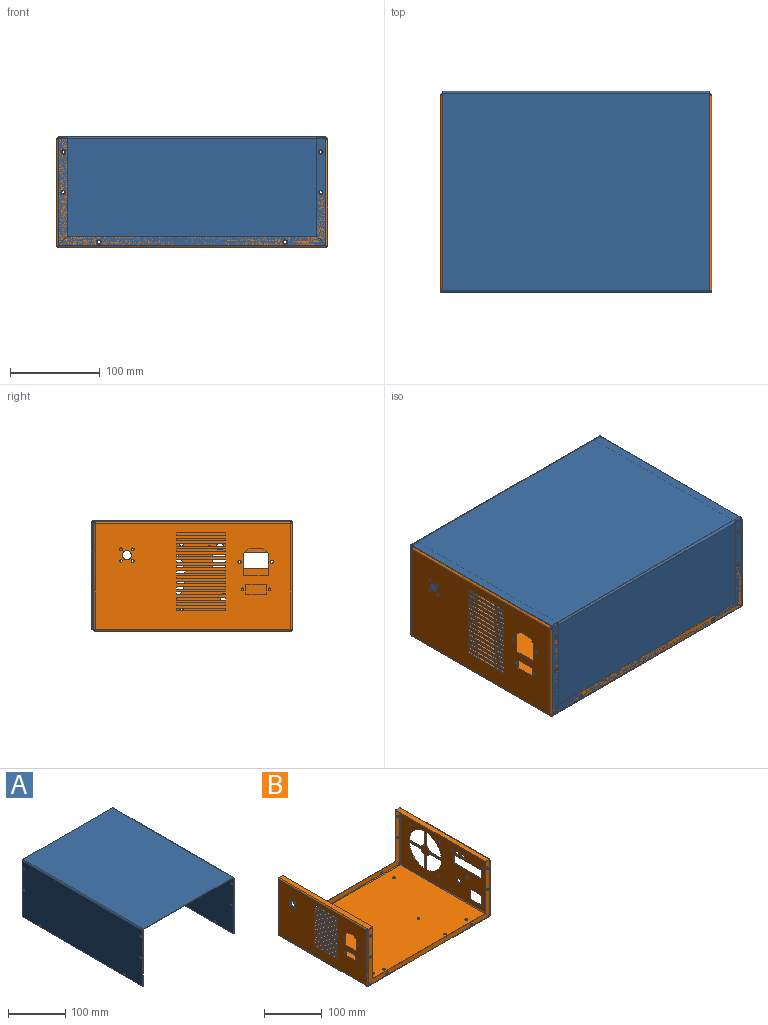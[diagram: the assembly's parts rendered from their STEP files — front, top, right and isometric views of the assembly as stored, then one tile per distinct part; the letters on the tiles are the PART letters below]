
ASSEMBLY  parts=2 mates=1
PART A: 34 faces, bbox 224.5x297.4x121 mm
  f0: plane 219.9x1mm, normal (0,-1,0), area 219.9mm2, adj f2,f3,f16,f31
  f1: plane 219.9x1mm, normal (0,1,0), area 219.9mm2, adj f2,f3,f15,f30
  f2: plane 297.4x219.9mm, normal (0,0,1), area 65398.3mm2, adj f0,f1,f17,f32
  f3: plane 297.4x219.9mm, normal (0,0,-1), area 65398.3mm2, adj f0,f1,f18,f33
  f4: plane 118.7x1mm, normal (0,-1,0), area 118.7mm2, adj f12,f13,f14,f16
  f5: plane 118.7x1mm, normal (0,1,0), area 118.7mm2, adj f12,f13,f14,f15
  f6: cylinder r=1.75mm len=3.5mm, axis (-1,0,0), area 11mm2, adj f13,f14
  f7: cylinder r=1.75mm len=3.5mm, axis (-1,0,0), area 11mm2, adj f13,f14
  f8: cylinder r=1.75mm len=3.5mm, axis (-1,0,0), area 11mm2, adj f13,f14
  f9: cylinder r=1.75mm len=3.5mm, axis (-1,0,0), area 11mm2, adj f13,f14
  f10: cylinder r=1.75mm len=3.5mm, axis (-1,0,0), area 11mm2, adj f13,f14
  f11: cylinder r=1.75mm len=3.5mm, axis (-1,0,0), area 11mm2, adj f13,f14
  f12: plane 297.4x1mm, normal (0,0,-1), area 297.4mm2, adj f4,f5,f13,f14
  f13: plane 297.4x118.7mm, normal (-1,0,0), area 35243.7mm2, adj f4,f5,f6,f7,f8,f9,f10,f11
  f14: plane 297.4x118.7mm, normal (1,0,0), area 35243.7mm2, adj f4,f5,f6,f7,f8,f9,f10,f11
  f15: plane 2.3x2.3mm, normal (0,1,0), area 2.8mm2, adj f1,f5,f17,f18
  f16: plane 2.3x2.3mm, normal (0,-1,0), area 2.8mm2, adj f0,f4,f17,f18
  f17: cylinder r=2.3mm len=297.4mm, axis (0,1,0), area 1074.5mm2, adj f2,f13,f15,f16
  f18: cylinder r=1.3mm len=297.4mm, axis (0,1,0), area 607.3mm2, adj f3,f14,f15,f16
  f19: plane 118.7x1mm, normal (0,-1,0), area 118.7mm2, adj f20,f28,f29,f31
  f20: plane 297.4x1mm, normal (0,0,-1), area 297.4mm2, adj f19,f21,f28,f29
  f21: plane 118.7x1mm, normal (0,1,0), area 118.7mm2, adj f20,f28,f29,f30
  f22: cylinder r=1.75mm len=3.5mm, axis (-1,0,0), area 11mm2, adj f28,f29
  f23: cylinder r=1.75mm len=3.5mm, axis (-1,0,0), area 11mm2, adj f28,f29
  f24: cylinder r=1.75mm len=3.5mm, axis (-1,0,0), area 11mm2, adj f28,f29
  f25: cylinder r=1.75mm len=3.5mm, axis (-1,0,0), area 11mm2, adj f28,f29
  f26: cylinder r=1.75mm len=3.5mm, axis (-1,0,0), area 11mm2, adj f28,f29
  f27: cylinder r=1.75mm len=3.5mm, axis (-1,0,0), area 11mm2, adj f28,f29
  f28: plane 297.4x118.7mm, normal (1,0,0), area 35243.7mm2, adj f19,f20,f21,f22,f23,f24,f25,f26
  f29: plane 297.4x118.7mm, normal (-1,0,0), area 35243.7mm2, adj f19,f20,f21,f22,f23,f24,f25,f26
  f30: plane 2.3x2.3mm, normal (0,1,0), area 2.8mm2, adj f1,f21,f32,f33
  f31: plane 2.3x2.3mm, normal (0,-1,0), area 2.8mm2, adj f0,f19,f32,f33
  f32: cylinder r=2.3mm len=297.4mm, axis (0,1,0), area 1074.5mm2, adj f2,f28,f30,f31
  f33: cylinder r=1.3mm len=297.4mm, axis (0,1,0), area 607.3mm2, adj f3,f29,f30,f31
PART B: 235 faces, bbox 302x222x122 mm
  f0: plane 1x0.01mm, normal (0,-1,0), area 0mm2, adj f82,f83,f85,f219
  f1: plane 1x0.01mm, normal (0,1,0), area 0mm2, adj f135,f174,f175,f195
  f2: plane 11.1x1mm, normal (0,1,0), area 11.1mm2, adj f3,f81,f82,f83
  f3: plane 22.3x1mm, normal (0,0,1), area 22.3mm2, adj f2,f4,f82,f83
  f4: plane 11.1x1mm, normal (0,-1,0), area 11.1mm2, adj f3,f81,f82,f83
  f5: plane 15.5x1mm, normal (0,0,-1), area 15.5mm2, adj f6,f80,f82,f83
  f6: plane 6x6mm, normal (0,0.71,-0.71), area 8.5mm2, adj f5,f7,f82,f83
  f7: plane 24x1mm, normal (0,1,0), area 24mm2, adj f6,f8,f82,f83
  f8: plane 27.5x1mm, normal (0,0,1), area 27.5mm2, adj f7,f9,f82,f83
  f9: plane 24x1mm, normal (0,-1,0), area 24mm2, adj f8,f80,f82,f83
  f10: plane 3x1mm, normal (0,-1,0), area 3mm2, adj f11,f79,f82,f83
  f11: plane 55x1mm, normal (0,0,-1), area 55mm2, adj f10,f12,f82,f83
  f12: plane 3x1mm, normal (0,1,0), area 3mm2, adj f11,f79,f82,f83
  f13: plane 3x1mm, normal (0,-1,0), area 3mm2, adj f14,f78,f82,f83
  f14: plane 55x1mm, normal (0,0,-1), area 55mm2, adj f13,f15,f82,f83
  f15: plane 3x1mm, normal (0,1,0), area 3mm2, adj f14,f78,f82,f83
  f16: plane 3x1mm, normal (0,-1,0), area 3mm2, adj f17,f77,f82,f83
  f17: plane 55x1mm, normal (0,0,-1), area 55mm2, adj f16,f18,f82,f83
  f18: plane 3x1mm, normal (0,1,0), area 3mm2, adj f17,f77,f82,f83
  f19: plane 3x1mm, normal (0,-1,0), area 3mm2, adj f20,f76,f82,f83
  f20: plane 55x1mm, normal (0,0,-1), area 55mm2, adj f19,f21,f82,f83
  f21: plane 3x1mm, normal (0,1,0), area 3mm2, adj f20,f76,f82,f83
  f22: plane 3x1mm, normal (0,-1,0), area 3mm2, adj f23,f75,f82,f83
  f23: plane 55x1mm, normal (0,0,-1), area 55mm2, adj f22,f24,f82,f83
  f24: plane 3x1mm, normal (0,1,0), area 3mm2, adj f23,f75,f82,f83
  f25: plane 3x1mm, normal (0,-1,0), area 3mm2, adj f26,f74,f82,f83
  f26: plane 55x1mm, normal (0,0,-1), area 55mm2, adj f25,f27,f82,f83
  f27: plane 3x1mm, normal (0,1,0), area 3mm2, adj f26,f74,f82,f83
  f28: plane 3x1mm, normal (0,-1,0), area 3mm2, adj f29,f73,f82,f83
  f29: plane 55x1mm, normal (0,0,-1), area 55mm2, adj f28,f30,f82,f83
  f30: plane 3x1mm, normal (0,1,0), area 3mm2, adj f29,f73,f82,f83
  f31: plane 3x1mm, normal (0,-1,0), area 3mm2, adj f32,f72,f82,f83
  f32: plane 55x1mm, normal (0,0,-1), area 55mm2, adj f31,f33,f82,f83
  f33: plane 3x1mm, normal (0,1,0), area 3mm2, adj f32,f72,f82,f83
  f34: plane 3x1mm, normal (0,-1,0), area 3mm2, adj f35,f71,f82,f83
  f35: plane 55x1mm, normal (0,0,-1), area 55mm2, adj f34,f36,f82,f83
  f36: plane 3x1mm, normal (0,1,0), area 3mm2, adj f35,f71,f82,f83
  f37: plane 3x1mm, normal (0,-1,0), area 3mm2, adj f38,f70,f82,f83
  f38: plane 55x1mm, normal (0,0,-1), area 55mm2, adj f37,f39,f82,f83
  f39: plane 3x1mm, normal (0,1,0), area 3mm2, adj f38,f70,f82,f83
  f40: plane 3x1mm, normal (0,-1,0), area 3mm2, adj f41,f69,f82,f83
  f41: plane 55x1mm, normal (0,0,-1), area 55mm2, adj f40,f42,f82,f83
  f42: plane 3x1mm, normal (0,1,0), area 3mm2, adj f41,f69,f82,f83
  f43: plane 3x1mm, normal (0,-1,0), area 3mm2, adj f44,f68,f82,f83
  f44: plane 55x1mm, normal (0,0,-1), area 55mm2, adj f43,f45,f82,f83
  f45: plane 3x1mm, normal (0,1,0), area 3mm2, adj f44,f68,f82,f83
  f46: plane 3x1mm, normal (0,-1,0), area 3mm2, adj f47,f67,f82,f83
  f47: plane 55x1mm, normal (0,0,-1), area 55mm2, adj f46,f48,f82,f83
  f48: plane 3x1mm, normal (0,1,0), area 3mm2, adj f47,f67,f82,f83
  f49: plane 3x1mm, normal (0,-1,0), area 3mm2, adj f50,f66,f82,f83
  f50: plane 55x1mm, normal (0,0,-1), area 55mm2, adj f49,f51,f82,f83
  f51: plane 3x1mm, normal (0,1,0), area 3mm2, adj f50,f66,f82,f83
  f52: plane 55x1mm, normal (0,0,1), area 55mm2, adj f53,f65,f82,f83
  f53: plane 3x1mm, normal (0,-1,0), area 3mm2, adj f52,f54,f82,f83
  f54: plane 55x1mm, normal (0,0,-1), area 55mm2, adj f53,f65,f82,f83
  f55: plane 1x0.01mm, normal (0,1,0), area 0mm2, adj f82,f83,f84,f231
  f56: cylinder r=1.4mm len=2.8mm, axis (-1,0,0), area 8.8mm2, adj f82,f83
  f57: cylinder r=1.4mm len=2.8mm, axis (-1,0,0), area 8.8mm2, adj f82,f83
  f58: cylinder r=1.5mm len=3mm, axis (-1,0,0), area 9.4mm2, adj f82,f83
  f59: cylinder r=1.5mm len=3mm, axis (-1,0,0), area 9.4mm2, adj f82,f83
  f60: cylinder r=1.5mm len=3mm, axis (-1,0,0), area 9.4mm2, adj f82,f83
  f61: cylinder r=1.5mm len=3mm, axis (-1,0,0), area 9.4mm2, adj f82,f83
  f62: cylinder r=5mm len=10mm, axis (-1,0,0), area 31.4mm2, adj f82,f83
  f63: cylinder r=1.75mm len=3.5mm, axis (-1,0,0), area 11mm2, adj f82,f83
  f64: cylinder r=1.75mm len=3.5mm, axis (-1,0,0), area 11mm2, adj f82,f83
  f65: plane 3x1mm, normal (0,1,0), area 3mm2, adj f52,f54,f82,f83
  f66: plane 55x1mm, normal (0,0,1), area 55mm2, adj f49,f51,f82,f83
  f67: plane 55x1mm, normal (0,0,1), area 55mm2, adj f46,f48,f82,f83
  f68: plane 55x1mm, normal (0,0,1), area 55mm2, adj f43,f45,f82,f83
  f69: plane 55x1mm, normal (0,0,1), area 55mm2, adj f40,f42,f82,f83
  f70: plane 55x1mm, normal (0,0,1), area 55mm2, adj f37,f39,f82,f83
  f71: plane 55x1mm, normal (0,0,1), area 55mm2, adj f34,f36,f82,f83
  f72: plane 55x1mm, normal (0,0,1), area 55mm2, adj f31,f33,f82,f83
  f73: plane 55x1mm, normal (0,0,1), area 55mm2, adj f28,f30,f82,f83
  f74: plane 55x1mm, normal (0,0,1), area 55mm2, adj f25,f27,f82,f83
  f75: plane 55x1mm, normal (0,0,1), area 55mm2, adj f22,f24,f82,f83
  f76: plane 55x1mm, normal (0,0,1), area 55mm2, adj f19,f21,f82,f83
  f77: plane 55x1mm, normal (0,0,1), area 55mm2, adj f16,f18,f82,f83
  f78: plane 55x1mm, normal (0,0,1), area 55mm2, adj f13,f15,f82,f83
  f79: plane 55x1mm, normal (0,0,1), area 55mm2, adj f10,f12,f82,f83
  f80: plane 6x6mm, normal (0,-0.71,-0.71), area 8.5mm2, adj f5,f9,f82,f83
  f81: plane 22.3x1mm, normal (0,0,-1), area 22.3mm2, adj f2,f4,f82,f83
  f82: plane 217.4x117.4mm, normal (-1,0,0), area 21872.9mm2, adj f0,f2,f3,f4,f5,f6,f7,f8
  f83: plane 217.4x117.4mm, normal (1,0,0), area 21872.9mm2, adj f0,f2,f3,f4,f5,f6,f7,f8
  f84: plane 2.3x2.3mm, normal (0,1,0), area 2.8mm2, adj f55,f86,f87,f100
  f85: plane 2.3x2.3mm, normal (0,-1,0), area 2.8mm2, adj f0,f86,f87,f101
  f86: cylinder r=2.3mm len=217.4mm, axis (0,1,0), area 785.4mm2, adj f82,f84,f85,f111
  f87: cylinder r=1.3mm len=217.4mm, axis (0,1,0), area 443.9mm2, adj f83,f84,f85,f112
  f88: plane 1.28x1mm, normal (-1,0,0), area 1.3mm2, adj f90,f93,f94,f95
  f89: plane 219.96x1mm, normal (1,0,0), area 220mm2, adj f90,f92,f93,f94
  f90: plane 9.7x1mm, normal (0,1,0), area 9.7mm2, adj f88,f89,f93,f94
  f91: plane 1.28x1mm, normal (-1,0,0), area 1.3mm2, adj f92,f93,f94,f96
  f92: plane 9.7x1mm, normal (0,-1,0), area 9.7mm2, adj f89,f91,f93,f94
  f93: plane 219.96x9.7mm, normal (0,0,1), area 2133.6mm2, adj f88,f89,f90,f91,f92,f97
  f94: plane 219.96x9.7mm, normal (0,0,-1), area 2133.6mm2, adj f88,f89,f90,f91,f92,f98
  f95: plane 2.3x2.3mm, normal (0,1,0), area 2.8mm2, adj f88,f97,f98,f232
  f96: plane 2.3x2.3mm, normal (0,-1,0), area 2.8mm2, adj f91,f97,f98,f220
  f97: cylinder r=2.3mm len=217.4mm, axis (0,1,0), area 785.4mm2, adj f82,f93,f95,f96
  f98: cylinder r=1.3mm len=217.4mm, axis (0,1,0), area 443.9mm2, adj f83,f94,f95,f96
  f99: plane 1x0.01mm, normal (0,-1,0), area 0mm2, adj f111,f112,f131,f136
  f100: plane 1x0.01mm, normal (0,1,0), area 0mm2, adj f84,f111,f112,f121
  f101: plane 1x0.01mm, normal (0,-1,0), area 0mm2, adj f85,f111,f112,f132
  f102: cylinder r=2.55mm len=5.1mm, axis (0,0,1), area 16mm2, adj f111,f112
  f103: cylinder r=2.55mm len=5.1mm, axis (0,0,1), area 16mm2, adj f111,f112
  f104: cylinder r=2.55mm len=5.1mm, axis (0,0,1), area 16mm2, adj f111,f112
  f105: cylinder r=2.55mm len=5.1mm, axis (0,0,1), area 16mm2, adj f111,f112
  f106: cylinder r=2.55mm len=5.1mm, axis (0,0,1), area 16mm2, adj f111,f112
  f107: cylinder r=2.55mm len=5.1mm, axis (0,0,1), area 16mm2, adj f111,f112
  f108: cylinder r=2.55mm len=5.1mm, axis (0,0,1), area 16mm2, adj f111,f112
  f109: cylinder r=2.55mm len=5.1mm, axis (0,0,1), area 16mm2, adj f111,f112
  f110: plane 1x0.01mm, normal (0,1,0), area 0mm2, adj f111,f112,f120,f135
  f111: plane 297.4x217.4mm, normal (0,0,-1), area 64491.3mm2, adj f86,f99,f100,f101,f102,f103,f104,f105
  f112: plane 297.4x217.4mm, normal (0,0,1), area 64491.3mm2, adj f87,f99,f100,f101,f102,f103,f104,f105
  f113: plane 277.97x1mm, normal (0,0,1), area 278mm2, adj f114,f117,f118,f119
  f114: plane 9.7x9.7mm, normal (0.71,0,0.71), area 13.7mm2, adj f113,f118,f119,f120
  f115: cylinder r=2.55mm len=5.1mm, axis (0,1,0), area 16mm2, adj f118,f119
  f116: cylinder r=2.55mm len=5.1mm, axis (0,1,0), area 16mm2, adj f118,f119
  f117: plane 9.7x9.7mm, normal (-0.71,0,0.71), area 13.7mm2, adj f113,f118,f119,f121
  f118: plane 297.37x9.7mm, normal (0,1,0), area 2749.6mm2, adj f113,f114,f115,f116,f117,f122
  f119: plane 297.37x9.7mm, normal (0,-1,0), area 2749.6mm2, adj f113,f114,f115,f116,f117,f123
  f120: plane 2.3x2.3mm, normal (1,0,0), area 2.8mm2, adj f110,f114,f122,f123
  f121: plane 2.3x2.3mm, normal (-1,0,0), area 2.8mm2, adj f100,f117,f122,f123
  f122: cylinder r=2.3mm len=297.37mm, axis (1,0,0), area 1074.4mm2, adj f111,f118,f120,f121
  f123: cylinder r=1.3mm len=297.37mm, axis (1,0,0), area 607.2mm2, adj f112,f119,f120,f121
  f124: plane 277.97x1mm, normal (0,0,1), area 278mm2, adj f125,f128,f129,f130
  f125: plane 9.7x9.7mm, normal (-0.71,0,0.71), area 13.7mm2, adj f124,f129,f130,f132
  f126: cylinder r=2.55mm len=5.1mm, axis (0,-1,0), area 16mm2, adj f129,f130
  f127: cylinder r=2.55mm len=5.1mm, axis (0,-1,0), area 16mm2, adj f129,f130
  f128: plane 9.7x9.7mm, normal (0.71,0,0.71), area 13.7mm2, adj f124,f129,f130,f131
  f129: plane 297.37x9.7mm, normal (0,-1,0), area 2749.6mm2, adj f124,f125,f126,f127,f128,f133
  f130: plane 297.37x9.7mm, normal (0,1,0), area 2749.6mm2, adj f124,f125,f126,f127,f128,f134
  f131: plane 2.3x2.3mm, normal (1,0,0), area 2.8mm2, adj f99,f128,f133,f134
  f132: plane 2.3x2.3mm, normal (-1,0,0), area 2.8mm2, adj f101,f125,f133,f134
  f133: cylinder r=2.3mm len=297.37mm, axis (1,0,0), area 1074.4mm2, adj f111,f129,f131,f132
  f134: cylinder r=1.3mm len=297.37mm, axis (1,0,0), area 607.2mm2, adj f112,f130,f131,f132
  f135: plane 2.3x2.3mm, normal (0,1,0), area 2.8mm2, adj f1,f110,f137,f138
  f136: plane 2.3x2.3mm, normal (0,-1,0), area 2.8mm2, adj f99,f137,f138,f139
  f137: cylinder r=2.3mm len=217.4mm, axis (0,1,0), area 785.4mm2, adj f111,f135,f136,f174
  f138: cylinder r=1.3mm len=217.4mm, axis (0,1,0), area 443.9mm2, adj f112,f135,f136,f175
  f139: plane 1x0.01mm, normal (0,-1,0), area 0mm2, adj f136,f174,f175,f207
  f140: plane 30.24x1mm, normal (0,0,1), area 30.2mm2, adj f141,f173,f174,f175
  f141: cylinder r=10mm len=7.18mm, axis (-1,0,0), area 10.7mm2, adj f140,f142,f174,f175
  f142: plane 30.24x1mm, normal (0,1,0), area 30.2mm2, adj f141,f173,f174,f175
  f143: plane 30.24x1mm, normal (0,-1,0), area 30.2mm2, adj f144,f172,f174,f175
  f144: cylinder r=10mm len=7.18mm, axis (-1,0,0), area 10.7mm2, adj f143,f145,f174,f175
  f145: plane 30.24x1mm, normal (0,0,1), area 30.2mm2, adj f144,f172,f174,f175
  f146: plane 30.24x1mm, normal (0,0,-1), area 30.2mm2, adj f147,f171,f174,f175
  f147: cylinder r=10mm len=7.18mm, axis (-1,0,0), area 10.7mm2, adj f146,f148,f174,f175
  f148: plane 30.24x1mm, normal (0,-1,0), area 30.2mm2, adj f147,f171,f174,f175
  f149: plane 30.24x1mm, normal (0,1,0), area 30.2mm2, adj f150,f170,f174,f175
  f150: cylinder r=10mm len=7.18mm, axis (-1,0,0), area 10.7mm2, adj f149,f151,f174,f175
  f151: plane 30.24x1mm, normal (0,0,-1), area 30.2mm2, adj f150,f170,f174,f175
  f152: plane 18x1mm, normal (0,-1,0), area 18mm2, adj f153,f165,f174,f175
  f153: plane 68x1mm, normal (0,0,1), area 68mm2, adj f152,f154,f174,f175
  f154: plane 18x1mm, normal (0,1,0), area 18mm2, adj f153,f165,f174,f175
  f155: plane 22x1mm, normal (0,-1,0), area 22mm2, adj f156,f164,f174,f175
  f156: plane 29x1mm, normal (0,0,1), area 29mm2, adj f155,f157,f174,f175
  f157: plane 22x1mm, normal (0,1,0), area 22mm2, adj f156,f164,f174,f175
  f158: cylinder r=1.75mm len=3.5mm, axis (-1,0,0), area 11mm2, adj f174,f175
  f159: cylinder r=1.75mm len=3.5mm, axis (-1,0,0), area 11mm2, adj f174,f175
  f160: cylinder r=4.75mm len=9.5mm, axis (-1,0,0), area 29.8mm2, adj f174,f175
  f161: cylinder r=3.25mm len=6.5mm, axis (-1,0,0), area 20.4mm2, adj f174,f175
  f162: cylinder r=4mm len=8mm, axis (-1,0,0), area 25.1mm2, adj f174,f175
  f163: cylinder r=4mm len=8mm, axis (-1,0,0), area 25.1mm2, adj f174,f175
  f164: plane 29x1mm, normal (0,0,-1), area 29mm2, adj f155,f157,f174,f175
  f165: plane 68x1mm, normal (0,0,-1), area 68mm2, adj f152,f154,f174,f175
  f166: cylinder r=2mm len=4mm, axis (-1,0,0), area 12.6mm2, adj f174,f175
  f167: cylinder r=2mm len=4mm, axis (-1,0,0), area 12.6mm2, adj f174,f175
  f168: cylinder r=2mm len=4mm, axis (-1,0,0), area 12.6mm2, adj f174,f175
  f169: cylinder r=2mm len=4mm, axis (-1,0,0), area 12.6mm2, adj f174,f175
  f170: cylinder r=40mm len=37.42mm, axis (-1,0,0), area 57.8mm2, adj f149,f151,f174,f175
  f171: cylinder r=40mm len=37.42mm, axis (-1,0,0), area 57.8mm2, adj f146,f148,f174,f175
  f172: cylinder r=40mm len=37.42mm, axis (-1,0,0), area 57.8mm2, adj f143,f145,f174,f175
  f173: cylinder r=40mm len=37.42mm, axis (-1,0,0), area 57.8mm2, adj f140,f142,f174,f175
  f174: plane 217.4x117.4mm, normal (1,0,0), area 19275.8mm2, adj f1,f137,f139,f140,f141,f142,f143,f144
  f175: plane 217.4x117.4mm, normal (-1,0,0), area 19275.8mm2, adj f1,f138,f139,f140,f141,f142,f143,f144
  f176: plane 1.28x1mm, normal (1,0,0), area 1.3mm2, adj f178,f181,f182,f184
  f177: plane 219.96x1mm, normal (-1,0,0), area 220mm2, adj f178,f180,f181,f182
  f178: plane 9.7x1mm, normal (0,-1,0), area 9.7mm2, adj f176,f177,f181,f182
  f179: plane 1.28x1mm, normal (1,0,0), area 1.3mm2, adj f180,f181,f182,f183
  f180: plane 9.7x1mm, normal (0,1,0), area 9.7mm2, adj f177,f179,f181,f182
  f181: plane 219.96x9.7mm, normal (0,0,1), area 2133.6mm2, adj f176,f177,f178,f179,f180,f185
  f182: plane 219.96x9.7mm, normal (0,0,-1), area 2133.6mm2, adj f176,f177,f178,f179,f180,f186
  f183: plane 2.3x2.3mm, normal (0,1,0), area 2.8mm2, adj f179,f185,f186,f196
  f184: plane 2.3x2.3mm, normal (0,-1,0), area 2.8mm2, adj f176,f185,f186,f208
  f185: cylinder r=2.3mm len=217.4mm, axis (0,1,0), area 785.4mm2, adj f174,f181,f183,f184
  f186: cylinder r=1.3mm len=217.4mm, axis (0,1,0), area 443.9mm2, adj f175,f182,f183,f184
  f187: plane 1.28x1mm, normal (1,0,0), area 1.3mm2, adj f189,f193,f194,f196
  f188: plane 108.97x1mm, normal (-1,0,0), area 109mm2, adj f189,f192,f193,f194
  f189: plane 9.7x1mm, normal (0,0,1), area 9.7mm2, adj f187,f188,f193,f194
  f190: cylinder r=2.55mm len=5.1mm, axis (0,1,0), area 16mm2, adj f193,f194
  f191: cylinder r=2.55mm len=5.1mm, axis (0,1,0), area 16mm2, adj f193,f194
  f192: plane 9.7x9.7mm, normal (-0.71,0,-0.71), area 13.7mm2, adj f188,f193,f194,f195
  f193: plane 118.67x9.7mm, normal (0,1,0), area 1063.2mm2, adj f187,f188,f189,f190,f191,f192,f197
  f194: plane 118.67x9.7mm, normal (0,-1,0), area 1063.2mm2, adj f187,f188,f189,f190,f191,f192,f198
  f195: plane 2.3x2.3mm, normal (0,0,-1), area 2.8mm2, adj f1,f192,f197,f198
  f196: plane 2.3x2.3mm, normal (0,0,1), area 2.8mm2, adj f183,f187,f197,f198
  f197: cylinder r=2.3mm len=117.39mm, axis (0,0,-1), area 424.1mm2, adj f174,f193,f195,f196
  f198: cylinder r=1.3mm len=117.39mm, axis (0,0,-1), area 239.7mm2, adj f175,f194,f195,f196
  f199: plane 108.97x1mm, normal (-1,0,0), area 109mm2, adj f200,f204,f205,f206
  f200: plane 9.7x9.7mm, normal (-0.71,0,-0.71), area 13.7mm2, adj f199,f205,f206,f207
  f201: plane 1.28x1mm, normal (1,0,0), area 1.3mm2, adj f204,f205,f206,f208
  f202: cylinder r=2.55mm len=5.1mm, axis (0,-1,0), area 16mm2, adj f205,f206
  f203: cylinder r=2.55mm len=5.1mm, axis (0,-1,0), area 16mm2, adj f205,f206
  f204: plane 9.7x1mm, normal (0,0,1), area 9.7mm2, adj f199,f201,f205,f206
  f205: plane 118.67x9.7mm, normal (0,-1,0), area 1063.2mm2, adj f199,f200,f201,f202,f203,f204,f209
  f206: plane 118.67x9.7mm, normal (0,1,0), area 1063.2mm2, adj f199,f200,f201,f202,f203,f204,f210
  f207: plane 2.3x2.3mm, normal (0,0,-1), area 2.8mm2, adj f139,f200,f209,f210
  f208: plane 2.3x2.3mm, normal (0,0,1), area 2.8mm2, adj f184,f201,f209,f210
  f209: cylinder r=2.3mm len=117.39mm, axis (0,0,-1), area 424.1mm2, adj f174,f205,f207,f208
  f210: cylinder r=1.3mm len=117.39mm, axis (0,0,-1), area 239.7mm2, adj f175,f206,f207,f208
  f211: plane 1.28x1mm, normal (-1,0,0), area 1.3mm2, adj f213,f217,f218,f220
  f212: plane 108.97x1mm, normal (1,0,0), area 109mm2, adj f213,f216,f217,f218
  f213: plane 9.7x1mm, normal (0,0,1), area 9.7mm2, adj f211,f212,f217,f218
  f214: cylinder r=2.55mm len=5.1mm, axis (0,-1,0), area 16mm2, adj f217,f218
  f215: cylinder r=2.55mm len=5.1mm, axis (0,-1,0), area 16mm2, adj f217,f218
  f216: plane 9.7x9.7mm, normal (0.71,0,-0.71), area 13.7mm2, adj f212,f217,f218,f219
  f217: plane 118.67x9.7mm, normal (0,-1,0), area 1063.2mm2, adj f211,f212,f213,f214,f215,f216,f221
  f218: plane 118.67x9.7mm, normal (0,1,0), area 1063.2mm2, adj f211,f212,f213,f214,f215,f216,f222
  f219: plane 2.3x2.3mm, normal (0,0,-1), area 2.8mm2, adj f0,f216,f221,f222
  f220: plane 2.3x2.3mm, normal (0,0,1), area 2.8mm2, adj f96,f211,f221,f222
  f221: cylinder r=2.3mm len=117.39mm, axis (0,0,-1), area 424.1mm2, adj f82,f217,f219,f220
  f222: cylinder r=1.3mm len=117.39mm, axis (0,0,-1), area 239.7mm2, adj f83,f218,f219,f220
  f223: plane 108.97x1mm, normal (1,0,0), area 109mm2, adj f224,f228,f229,f230
  f224: plane 9.7x9.7mm, normal (0.71,0,-0.71), area 13.7mm2, adj f223,f229,f230,f231
  f225: plane 1.28x1mm, normal (-1,0,0), area 1.3mm2, adj f228,f229,f230,f232
  f226: cylinder r=2.55mm len=5.1mm, axis (0,1,0), area 16mm2, adj f229,f230
  f227: cylinder r=2.55mm len=5.1mm, axis (0,1,0), area 16mm2, adj f229,f230
  f228: plane 9.7x1mm, normal (0,0,1), area 9.7mm2, adj f223,f225,f229,f230
  f229: plane 118.67x9.7mm, normal (0,1,0), area 1063.2mm2, adj f223,f224,f225,f226,f227,f228,f233
  f230: plane 118.67x9.7mm, normal (0,-1,0), area 1063.2mm2, adj f223,f224,f225,f226,f227,f228,f234
  f231: plane 2.3x2.3mm, normal (0,0,-1), area 2.8mm2, adj f55,f224,f233,f234
  f232: plane 2.3x2.3mm, normal (0,0,1), area 2.8mm2, adj f95,f225,f233,f234
  f233: cylinder r=2.3mm len=117.39mm, axis (0,0,-1), area 424.1mm2, adj f82,f229,f231,f232
  f234: cylinder r=1.3mm len=117.39mm, axis (0,0,-1), area 239.7mm2, adj f83,f230,f231,f232
PLACE A rot(axis=(0,0,1),90deg) t=(-188.35,-138.03,-191.62)mm
PLACE B t=(-189.65,-138.03,-192.62)mm
MATE fastened A.f6 <-> B.f215  axis (0,-1,0) through (-183,-139.03,-87.62)mm
